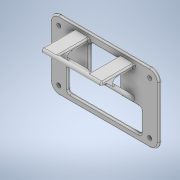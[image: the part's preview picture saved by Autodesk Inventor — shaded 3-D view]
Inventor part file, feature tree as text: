
AUTODESK INVENTOR PART (.ipt)
format: ipt  version: 2020.3 (Build 243373000, 373)  size: 538,624 bytes
history: native  units: mm
features: fillet x8, extrude x7, sketch x7, pattern_linear x1
ambient origin geometry x8: Origin, YZ Plane, XZ Plane, XY Plane, X Axis, Y Axis, Z Axis, Center Point
bodies: Solid1 (feature_tree)
feature tree (23):
  extrude  "Extrusion1"  Depth=38.8mm
  extrude  "Extrusion2"  Depth=3.0mm
  extrude  "Extrusion3"  Depth=3.0mm
  extrude  "Extrusion4"  Depth=2.5mm TaperAngle=0.0deg
  fillet  "Fillet1"  Radius=45.0mm
  extrude  "Extrusion5"  Depth=3.0mm
  fillet  "Fillet2"  Radius=25.0mm
  pattern_linear  "Rectangular Pattern1"  Spacing1=45.0deg  [1 undecoded]
  extrude  "Extrusion6"  Depth=3.0mm
  fillet  "Fillet3"  Radius=30.0mm
  fillet  "Fillet4"  Radius=22.5mm
  fillet  "Fillet5"  Radius=30.0mm
  fillet  "Fillet6"  Radius=2.0mm
  extrude  "Extrusion7"  Depth=1.0mm
  fillet  "Fillet7"  Radius=7.0mm
  fillet  "Fillet8"  Radius=3.0mm
  sketch  "Sketch1"  dims[d0=68.0mm d1=38.8mm]
  sketch  "Sketch2"  dims[d2=3.0mm d3=3.0mm]
  sketch  "Sketch3"  dims[d4=3.0mm d5=3.0mm]
  sketch  "Sketch4"  dims[d6=6.5mm d7=2.5mm d8=0.0mm d9=45.0mm]
  sketch  "Sketch7"  dims[d10=3.0mm d11=3.0mm d12=25.0mm d13=0.0mm]
  sketch  "Sketch8"  dims[d14=3.0mm]
  sketch  "Sketch9"  dims[d15=3.0mm d16=45.0deg d17=3.0mm d18=30.0mm d19=0.0mm d20=22.5mm d21=30.0mm d22=0.0mm d23=2.0mm d24=1.5mm d25=7.0mm d26=3.0mm d27=1.0mm d28=0.0mm d29=20.0mm d31=68.0mm d32=20.0mm d34=38.8mm d35=6.5mm d36=1.0mm d37=1.5mm d38=0.0mm d39=0.0mm d40=45.0mm d41=1.5mm d42=1.5mm d43=1.5mm d44=1.0mm d45=5.0mm d46=5.0mm d47=5.0mm d48=1.0mm d49=1.0mm d50=0.0mm d51=2.0mm d52=1.0mm]
note: 1 required parameter value undecoded (feature->parameter linkage not recoverable at this tier; creation-order binding heuristic only, values carry confidence <= 0.55)
